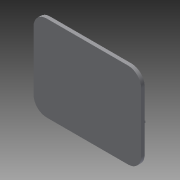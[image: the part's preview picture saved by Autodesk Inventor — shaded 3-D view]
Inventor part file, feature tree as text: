
AUTODESK INVENTOR PART (.ipt)
format: ipt  version: 2014 (Build 180170000, 170)  size: 326,144 bytes
history: native  units: mm
features: extrude x2, sketch x2, fillet x1
ambient origin geometry x8: Origin, YZ Plane, XZ Plane, XY Plane, X Axis, Y Axis, Z Axis, Center Point
bodies: Solid1 (feature_tree)
feature tree (5):
  extrude  "Extrusion1"  Depth=19.6mm
  extrude  "Extrusion2"  Depth=3.0mm TaperAngle=0.0deg
  fillet  "Fillet1"  Radius=3.0mm
  sketch  "Sketch1"  dims[d0=24.6mm d1=19.6mm]
  sketch  "Sketch2"  dims[d2=0.8mm d3=0.0mm d4=0.4mm d5=0.0mm d6=3.0mm]
